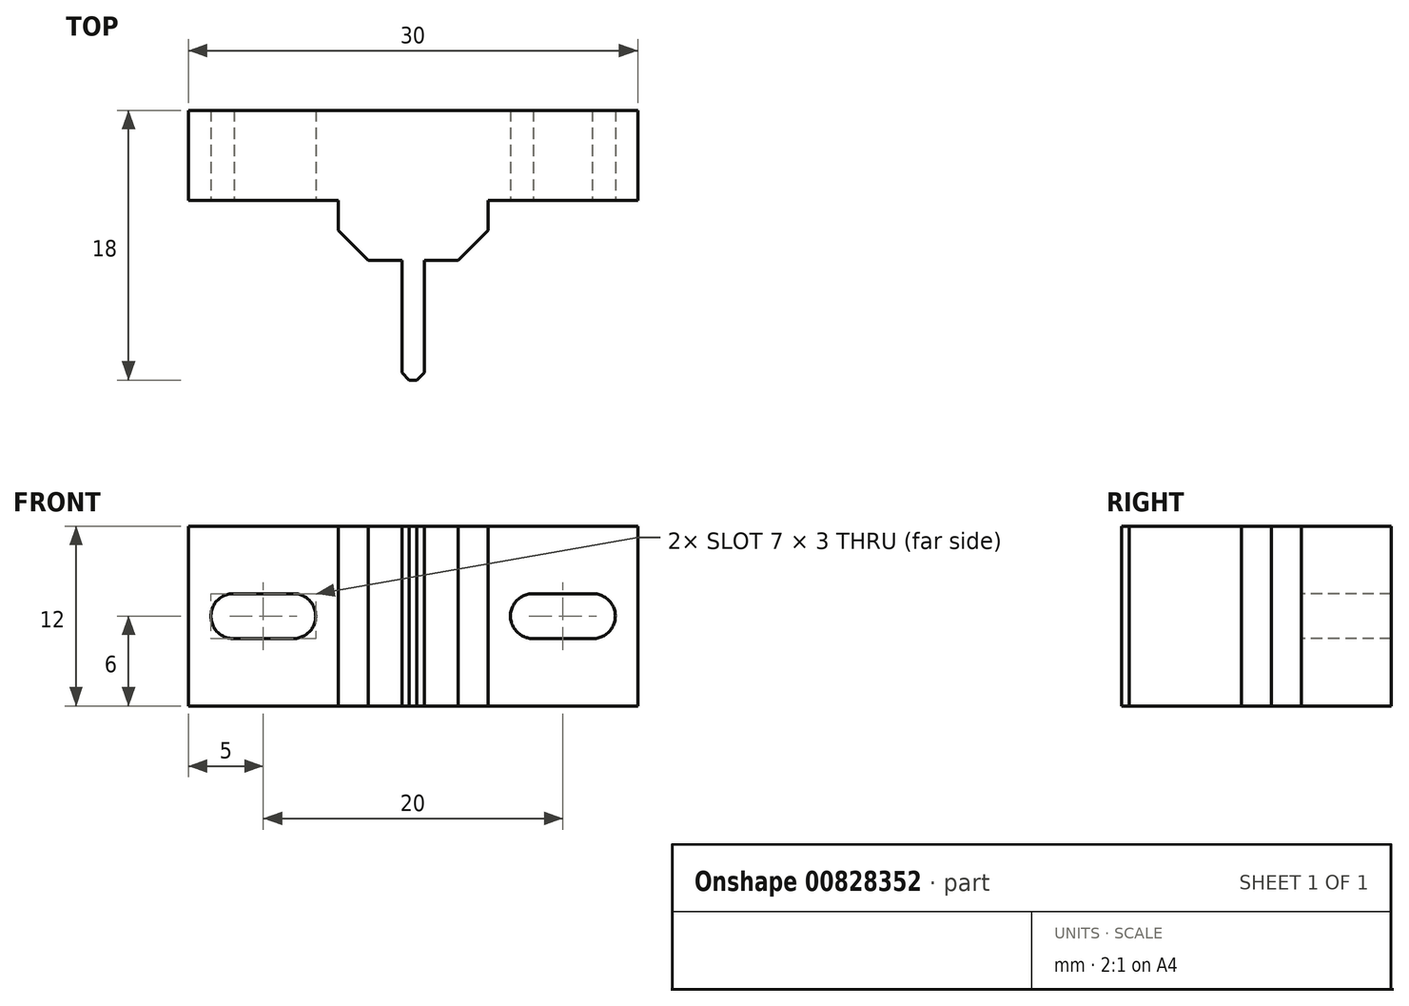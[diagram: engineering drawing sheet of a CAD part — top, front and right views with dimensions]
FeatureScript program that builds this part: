
annotation { "Feature Type Name" : "Feature", "Feature Type Description" : "" }
export const myFeature = defineFeature(function(context is Context, id is Id, definition is map)
    precondition{}
    {
        {
            var Q0;
            Q0=qCreatedBy(makeId("Front.planeOp"),FACE);
            var sketch = newSketch(context, id + "F0", { "sketchPlane" : qUnion([Q0])});
            skLineSegment(sketch, "E0.bottom", {"start": v(-15, 6) * mm, "end": v(15, 6) * mm});
            skLineSegment(sketch, "E0.top", {"start": v(-15, -6) * mm, "end": v(15, -6) * mm});
            skLineSegment(sketch, "E0.left", {"start": v(-15, 6) * mm, "end": v(-15, -6) * mm});
            skLineSegment(sketch, "E0.right", {"start": v(15, 6) * mm, "end": v(15, -6) * mm});
            skPoint(sketch, "E0.middle", {"position": v(0, 0) * mm});
            skSolve(sketch);
        }
        {
            var Q0;
            Q0 = qSketchRegion(id + "F0", true);
            extrude(context, id + "F1", {"entities" : qUnion([Q0]), "depth" : 6 * mm, "offsetDistance" : 25 * mm});
        }
        {
            var Q0;
            Q0=makeQuery(id+"F1.opExtrude","CAP_FACE",FACE,{"disambiguationData":[OSD([sQuery(id+"F0.wireOp",EDGE,"E0.bottom"),sQuery(id+"F0.wireOp",EDGE,"E0.top"),sQuery(id+"F0.wireOp",EDGE,"E0.left"),sQuery(id+"F0.wireOp",EDGE,"E0.right")])],"isStart":false});
            var sketch = newSketch(context, id + "F2", { "sketchPlane" : qUnion([Q0])});
            skLineSegment(sketch, "E1.bottom", {"start": v(-5, 6) * mm, "end": v(5, 6) * mm});
            skLineSegment(sketch, "E1.top", {"start": v(-5, -6) * mm, "end": v(5, -6) * mm});
            skLineSegment(sketch, "E1.left", {"start": v(-5, 6) * mm, "end": v(-5, -6) * mm});
            skLineSegment(sketch, "E1.right", {"start": v(5, 6) * mm, "end": v(5, -6) * mm});
            skPoint(sketch, "E1.middle", {"position": v(0, 0) * mm});
            skSolve(sketch);
        }
        {
            var Q0;
            Q0 = qSketchRegion(id + "F2", true);
            extrude(context, id + "F3", {"entities" : qUnion([Q0]), "operationType" : NewBodyOperationType.ADD, "depth" : 4 * mm, "offsetDistance" : 25 * mm});
        }
        {
            var Q0;
            Q0=makeQuery(id+"F3.opExtrude","CAP_FACE",FACE,{"disambiguationData":[OSD([sQuery(id+"F2.wireOp",EDGE,"E1.bottom"),sQuery(id+"F2.wireOp",EDGE,"E1.top"),sQuery(id+"F2.wireOp",EDGE,"E1.left"),sQuery(id+"F2.wireOp",EDGE,"E1.right")])],"isStart":false});
            var sketch = newSketch(context, id + "F4", { "sketchPlane" : qUnion([Q0])});
            skLineSegment(sketch, "E2.bottom", {"start": v(-0.75, 6) * mm, "end": v(0.75, 6) * mm});
            skLineSegment(sketch, "E2.top", {"start": v(-0.75, -6) * mm, "end": v(0.75, -6) * mm});
            skLineSegment(sketch, "E2.left", {"start": v(-0.75, 6) * mm, "end": v(-0.75, -6) * mm});
            skLineSegment(sketch, "E2.right", {"start": v(0.75, 6) * mm, "end": v(0.75, -6) * mm});
            skPoint(sketch, "E2.middle", {"position": v(0, 0) * mm});
            skSolve(sketch);
        }
        {
            var Q0;
            Q0 = qSketchRegion(id + "F4", true);
            extrude(context, id + "F5", {"entities" : qUnion([Q0]), "operationType" : NewBodyOperationType.ADD, "depth" : 8 * mm, "offsetDistance" : 25 * mm});
        }
        {
            var Q0;
            Q0=makeQuery(id+"F3.opExtrude","CAP_EDGE",EDGE,{"disambiguationData":[OSD([sQuery(id+"F2.wireOp",EDGE,"E1.left")])],"isStart":false});
            var Q1;
            Q1=makeQuery(id+"F3.opExtrude","CAP_EDGE",EDGE,{"disambiguationData":[OSD([sQuery(id+"F2.wireOp",EDGE,"E1.right")])],"isStart":false});
            chamfer(context, id + "F6", {"entities" : qUnion([Q0, Q1]), "width" : 2 * mm, "tangentPropagation" : true});
        }
        {
            var Q0;
            Q0=makeQuery(id+"F5.opExtrude","CAP_EDGE",EDGE,{"disambiguationData":[OSD([sQuery(id+"F4.wireOp",EDGE,"E2.left")])],"isStart":false});
            var Q1;
            Q1=makeQuery(id+"F5.opExtrude","CAP_EDGE",EDGE,{"disambiguationData":[OSD([sQuery(id+"F4.wireOp",EDGE,"E2.right")])],"isStart":false});
            chamfer(context, id + "F7", {"entities" : qUnion([Q0, Q1]), "width" : .5 * mm, "tangentPropagation" : true});
        }
        {
            var Q0;
            {var subQ0=sQuery(id+"F0.wireOp",EDGE,"E0.left");var subQ1=sQuery(id+"F0.wireOp",EDGE,"E0.top");var subQ2=sQuery(id+"F0.wireOp",EDGE,"E0.bottom");Q0=makeQuery(id+"F3.boolean.opBoolean","SPLIT",FACE,{"disambiguationData":[TD([makeQuery(id+"F1.opExtrude","SWEPT_FACE",FACE,{"disambiguationData":[OSD([subQ0])]})])],"derivedFrom":makeQuery(id+"F1.opExtrude","CAP_FACE",FACE,{"disambiguationData":[OSD([subQ2,subQ1,subQ0,sQuery(id+"F0.wireOp",EDGE,"E0.right")])],"isStart":false})});}
            var sketch = newSketch(context, id + "F8", { "sketchPlane" : qUnion([Q0])});
            skPoint(sketch, "E3.positionSnap0", {"position": v(-10, 6) * mm});
            skPoint(sketch, "E3.positionSnap1", {"position": v(-15, 0) * mm});
            skSolve(sketch);
        }
        {
            var Q0;
            {var subQ0=sQuery(id+"F0.wireOp",EDGE,"E0.top");var subQ1=sQuery(id+"F0.wireOp",EDGE,"E0.right");var subQ2=sQuery(id+"F0.wireOp",EDGE,"E0.bottom");Q0=makeQuery(id+"F3.boolean.opBoolean","SPLIT",FACE,{"disambiguationData":[TD([makeQuery(id+"F1.opExtrude","SWEPT_FACE",FACE,{"disambiguationData":[OSD([subQ1])]})])],"derivedFrom":makeQuery(id+"F1.opExtrude","CAP_FACE",FACE,{"disambiguationData":[OSD([subQ2,subQ0,sQuery(id+"F0.wireOp",EDGE,"E0.left"),subQ1])],"isStart":false})});}
            var sketch = newSketch(context, id + "F9", { "sketchPlane" : qUnion([Q0])});
            skPoint(sketch, "E4.positionSnap0", {"position": v(15, 0) * mm});
            skPoint(sketch, "E4.positionSnap1", {"position": v(10, 6) * mm});
            skPoint(sketch, "E5", {"position": v(8, 0) * mm});
            skPoint(sketch, "E6", {"position": v(12, 0) * mm});
            skCircle(sketch, "E7", {"center": v(8, 0) * mm, "radius": 1.5 * mm});
            skCircle(sketch, "E8", {"center": v(12, 0) * mm, "radius": 1.5 * mm});
            skLineSegment(sketch, "E9", {"start": v(7.97, 1.5) * mm, "end": v(11.97, 1.5) * mm});
            skLineSegment(sketch, "E10", {"start": v(8, -1.5) * mm, "end": v(12, -1.5) * mm});
            skSolve(sketch);
        }
        {
            var Q0;
            Q0 = qSketchRegion(id + "F9", true);
            extrude(context, id + "F10", {"entities" : qUnion([Q0]), "operationType" : NewBodyOperationType.REMOVE, "endBound" : BoundingType.UP_TO_NEXT, "oppositeDirection" : true, "depth" : 25 * mm, "offsetDistance" : 25 * mm});
        }
        {
            var Q0;
            {var subQ0=sQuery(id+"F0.wireOp",EDGE,"E0.left");Q0=makeQuery(id+"F8.imprint","IMPRINT",FACE,{"disambiguationData":[TD([[makeQuery(id+"F8.imprint","IMPRINT",EDGE,{"derivedFrom":makeQuery(id+"F1.opExtrude","CAP_EDGE",EDGE,{"disambiguationData":[OSD([subQ0])],"isStart":false})}),1.0]])]});}
            var sketch = newSketch(context, id + "F11", { "sketchPlane" : qUnion([Q0])});
            skPoint(sketch, "E11", {"position": v(-12, 0) * mm});
            skPoint(sketch, "E12", {"position": v(-8, 0) * mm});
            skCircle(sketch, "E13", {"center": v(-12, 0) * mm, "radius": 1.5 * mm});
            skCircle(sketch, "E14", {"center": v(-8, 0) * mm, "radius": 1.5 * mm});
            skLineSegment(sketch, "E15", {"start": v(-12.05, 1.5) * mm, "end": v(-8, 1.5) * mm});
            skLineSegment(sketch, "E16", {"start": v(-11.95, -1.5) * mm, "end": v(-8, -1.5) * mm});
            skSolve(sketch);
        }
        {
            var Q0;
            Q0 = qSketchRegion(id + "F11", true);
            extrude(context, id + "F12", {"entities" : qUnion([Q0]), "operationType" : NewBodyOperationType.REMOVE, "endBound" : BoundingType.UP_TO_NEXT, "oppositeDirection" : true, "depth" : 25 * mm, "offsetDistance" : 25 * mm});
        }
    });
